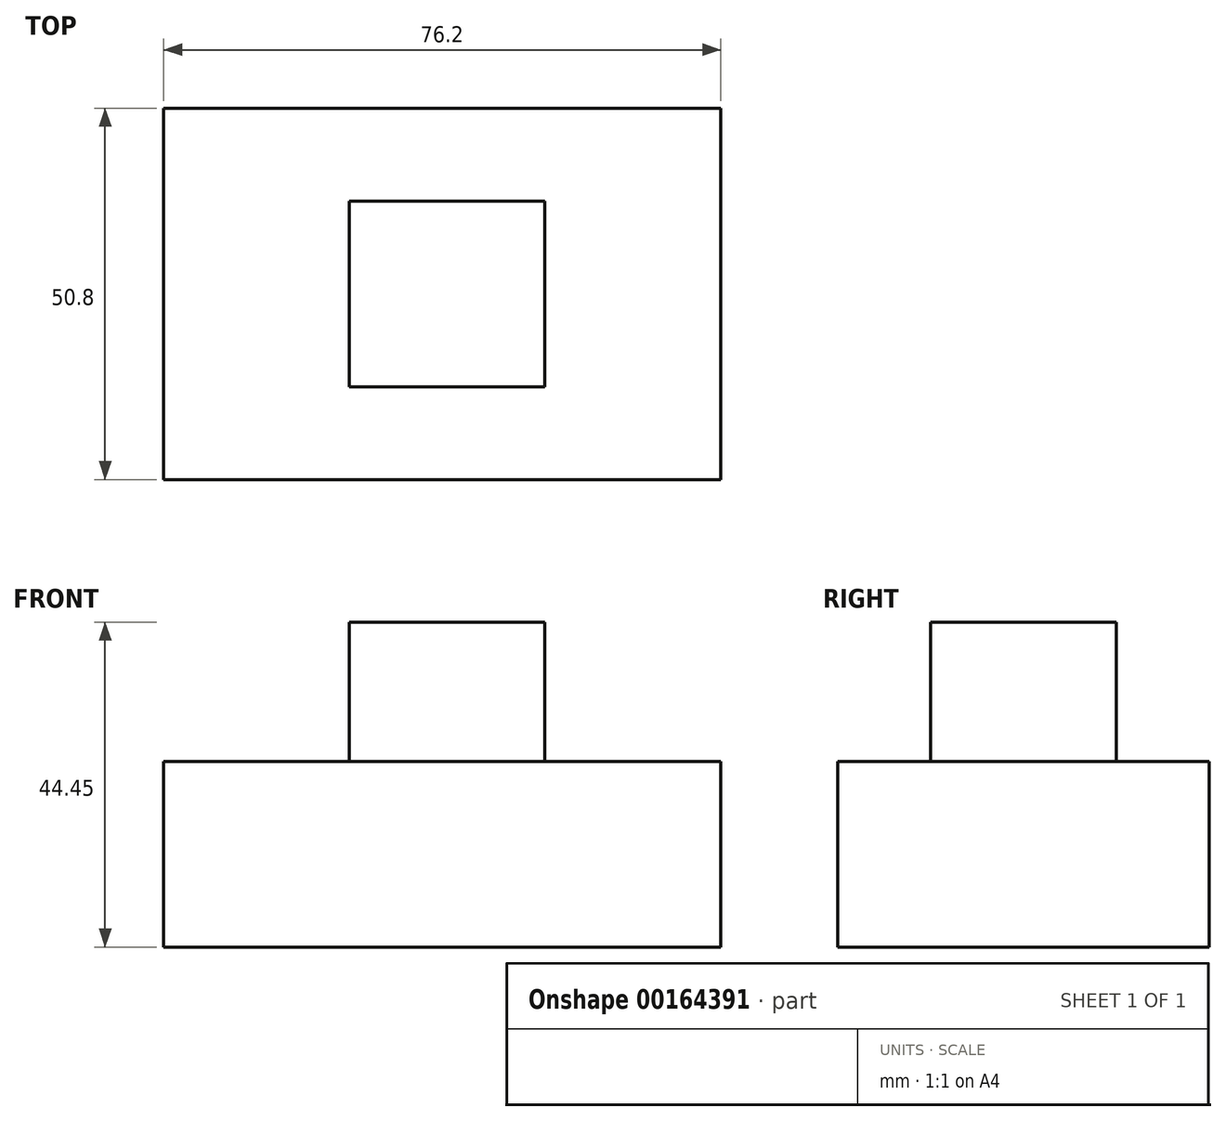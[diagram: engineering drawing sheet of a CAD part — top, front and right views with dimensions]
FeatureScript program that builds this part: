
annotation { "Feature Type Name" : "Feature", "Feature Type Description" : "" }
export const myFeature = defineFeature(function(context is Context, id is Id, definition is map)
    precondition{}
    {
        {
            var Q0;
            Q0=qCreatedBy(makeId("Top.planeOp"),FACE);
            var sketch = newSketch(context, id + "F0", { "sketchPlane" : qUnion([Q0])});
            skLineSegment(sketch, "E0.bottom", {"start": v(0, 0) * mm, "end": v(76.2, 0) * mm});
            skLineSegment(sketch, "E0.top", {"start": v(0, -50.8) * mm, "end": v(76.2, -50.8) * mm});
            skLineSegment(sketch, "E0.left", {"start": v(0, 0) * mm, "end": v(0, -50.8) * mm});
            skLineSegment(sketch, "E0.right", {"start": v(76.2, 0) * mm, "end": v(76.2, -50.8) * mm});
            skSolve(sketch);
        }
        {
            var Q0;
            Q0=makeQuery(id+"F0.imprint","IMPRINT",FACE,{"disambiguationData":[TD([[makeQuery(id+"F0.imprint","IMPRINT",EDGE,{"derivedFrom":sQuery(id+"F0.wireOp",EDGE,"E0.bottom")}),-1.0]])]});
            extrude(context, id + "F1", {"entities" : qUnion([Q0]), "depth" : 25.4 * mm});
        }
        {
            var Q0;
            Q0=qCreatedBy(makeId("Top.planeOp"),FACE);
            var sketch = newSketch(context, id + "F2", { "sketchPlane" : qUnion([Q0])});
            skLineSegment(sketch, "E1.bottom", {"start": v(25.4, -12.7) * mm, "end": v(52.15, -12.7) * mm});
            skLineSegment(sketch, "E1.top", {"start": v(25.4, -38.1) * mm, "end": v(52.15, -38.1) * mm});
            skLineSegment(sketch, "E1.left", {"start": v(25.4, -12.7) * mm, "end": v(25.4, -38.1) * mm});
            skLineSegment(sketch, "E1.right", {"start": v(52.15, -12.7) * mm, "end": v(52.15, -38.1) * mm});
            skSolve(sketch);
        }
        {
            var Q0;
            Q0=makeQuery(id+"F2.imprint","IMPRINT",FACE,{"disambiguationData":[TD([[makeQuery(id+"F2.imprint","IMPRINT",EDGE,{"derivedFrom":sQuery(id+"F2.wireOp",EDGE,"E1.bottom")}),-1.0]])]});
            extrude(context, id + "F3", {"entities" : qUnion([Q0]), "operationType" : NewBodyOperationType.ADD, "depth" : 44.45 * mm});
        }
    });
